# Revit family: LXEM
name_source: partatom
category: Lighting Fixtures
units: mm (PartAtom-declared; Revit-internal decimal feet)

## family parameters
Cut with Voids When Loaded = No
Host = Face
Light Source = Yes
OmniClass Number = 23.80.70.11
OmniClass Title = Luminaries for Internal Lighting
Part Type = Normal
Room Calculation Point = No
Round Connector Dimension = Use Diameter
Shared = Yes

## types (1)
- LXEM4-40XL-RFA-EU
    Apparent Load = 0 VA
    Backbox = White
    Color Filter = 16777215
    Default Elevation = 4.0'
    Description = LXEM is a multi-functional enclosed LED product which serves rugged to severe conditions as well as food service areas
    Dimming Lamp Color Temperature Shift = <None>
    Driver = Fixed Output
    Emit from Line Length = 2.0'
    Glass = White Glass
    Lamp = LED Lamp
    Lumen Output = Xtra High Lumen
    Manufacturer = Columbia Lighting
    Model = LXEM
    Nominal Watts = 102 W
    Photometric Web File = LXEM4-40XL-RFA-EU.ies
    Row Length = 4.0'
    Shielding = Ribbed Frosted Acrylic
    Tilt Angle = -90.00°
    URL = www.currentlighting.com/columbialighting
    Voltage = 120 V

## geometry (parser evidence)
native form markers: Blend x1, Sweep x3
no freeform markers — native parametric forms only
